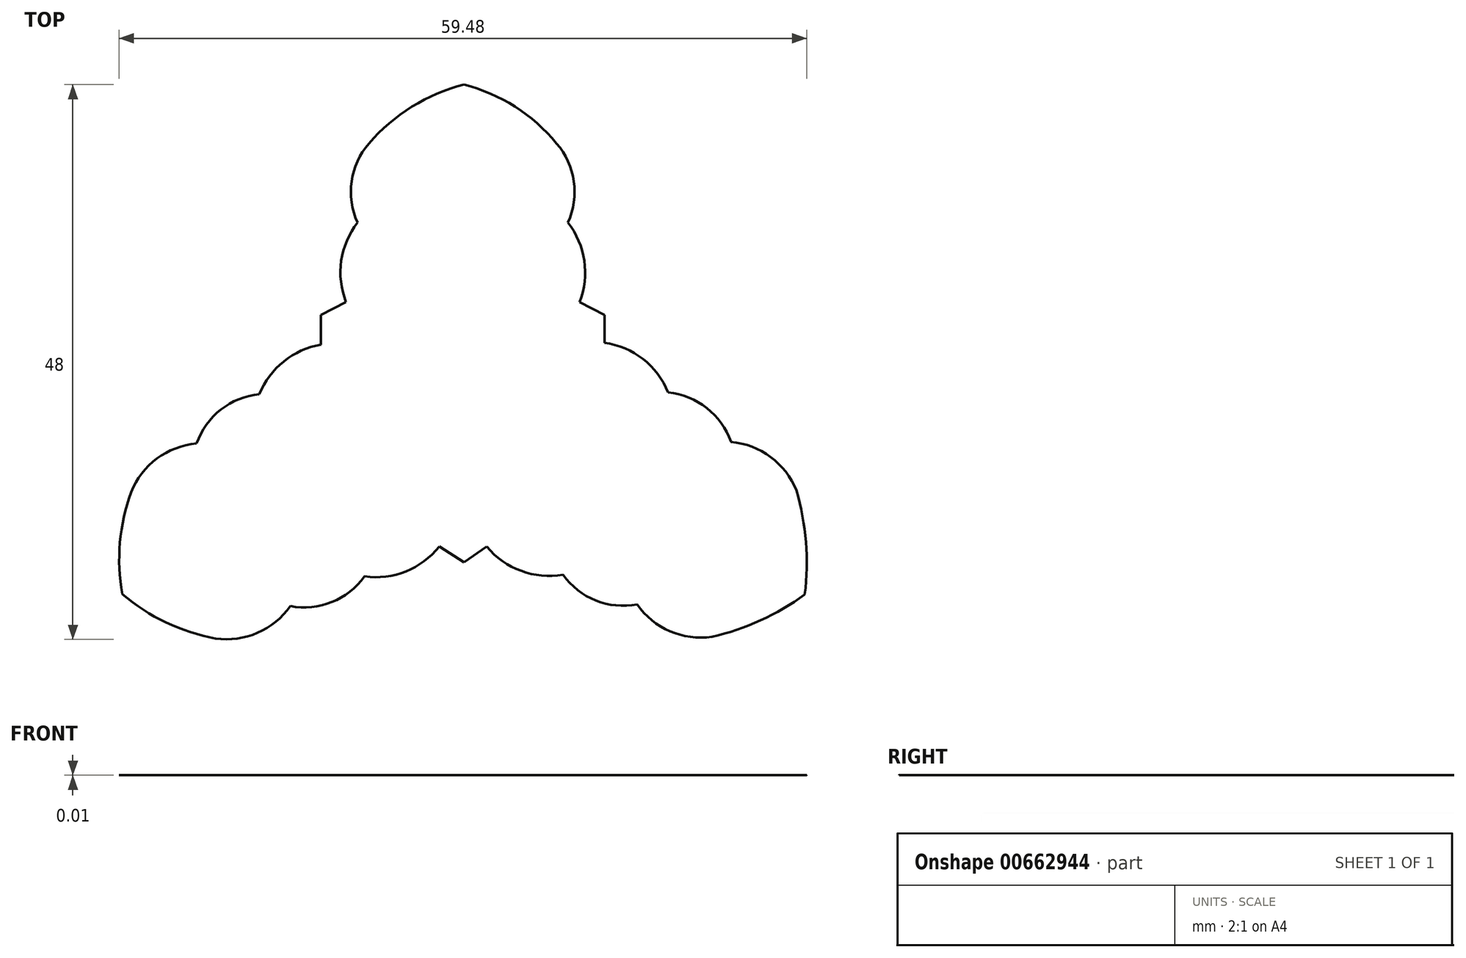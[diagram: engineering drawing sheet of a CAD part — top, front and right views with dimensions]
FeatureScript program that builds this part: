
annotation { "Feature Type Name" : "Feature", "Feature Type Description" : "" }
export const myFeature = defineFeature(function(context is Context, id is Id, definition is map)
    precondition{}
    {
        {
            var Q0;
            Q0=qCreatedBy(makeId("Top.planeOp"),FACE);
            var sketch = newSketch(context, id + "F0", { "sketchPlane" : qUnion([Q0])});
            skPoint(sketch, "E0.center", {"position": v(0, 0) * mm});
            skArc(sketch, "E1", {"start": v(-8.23, 21.98) * mm, "mid": v(-9.72, 18.7) * mm, "end": v(-9.2, 15.13) * mm});
            skArc(sketch, "E2", {"start": v(-9.2, 15.13) * mm, "mid": v(-10.62, 11.82) * mm, "end": v(-10.2, 8.25) * mm});
            skLineSegment(sketch, "E3", {"start": v(-10.2, 8.25) * mm, "end": v(-12.37, 7.15) * mm});
            skLineSegment(sketch, "E4", {"start": v(-12.37, 7.15) * mm, "end": v(-12.37, 4.64) * mm});
            skLineSegment(sketch, "E5.MirrorCS", {"start": v(12.16, 7.15) * mm, "end": v(12.16, 4.64) * mm});
            skLineSegment(sketch, "E6.MirrorCS", {"start": v(10, 8.25) * mm, "end": v(12.16, 7.15) * mm});
            skArc(sketch, "E7.MirrorCS", {"start": v(9, 15.13) * mm, "mid": v(10.4, 11.82) * mm, "end": v(10, 8.25) * mm});
            skArc(sketch, "E8.MirrorCS", {"start": v(8.01, 21.98) * mm, "mid": v(9.5, 18.7) * mm, "end": v(9, 15.13) * mm});
            skArc(sketch, "E9", {"start": v(28.76, -8.05) * mm, "mid": v(26.53, -5.15) * mm, "end": v(23.1, -3.85) * mm});
            skArc(sketch, "E10", {"start": v(23.1, -3.85) * mm, "mid": v(21, -0.92) * mm, "end": v(17.66, 0.43) * mm});
            skArc(sketch, "E11", {"start": v(17.66, 0.43) * mm, "mid": v(15.48, 3.32) * mm, "end": v(12.16, 4.74) * mm});
            skArc(sketch, "E12.MirrorCS", {"start": v(8.56, -15.34) * mm, "mid": v(4.94, -15) * mm, "end": v(1.97, -12.9) * mm});
            skArc(sketch, "E13.MirrorCS", {"start": v(14.98, -17.91) * mm, "mid": v(11.4, -17.56) * mm, "end": v(8.56, -15.34) * mm});
            skArc(sketch, "E14.MirrorCS", {"start": v(21.45, -20.71) * mm, "mid": v(17.82, -20.23) * mm, "end": v(14.98, -17.91) * mm});
            skLineSegment(sketch, "E15", {"start": v(1.97, -12.9) * mm, "end": v(0, -14.26) * mm});
            skLineSegment(sketch, "E16", {"start": v(0, -14.26) * mm, "end": v(-2.14, -12.9) * mm});
            skArc(sketch, "E17", {"start": v(-21.5, -20.86) * mm, "mid": v(-17.86, -20.37) * mm, "end": v(-15.02, -18.05) * mm});
            skArc(sketch, "E18", {"start": v(-15.02, -18.05) * mm, "mid": v(-11.43, -17.7) * mm, "end": v(-8.6, -15.48) * mm});
            skArc(sketch, "E19", {"start": v(-8.6, -15.48) * mm, "mid": v(-5.03, -15.05) * mm, "end": v(-2.14, -12.9) * mm});
            skArc(sketch, "E20.MirrorCS", {"start": v(-17.7, 0.28) * mm, "mid": v(-15.6, 3.12) * mm, "end": v(-12.37, 4.57) * mm});
            skArc(sketch, "E21.MirrorCS", {"start": v(-23.14, -4) * mm, "mid": v(-21.05, -1.06) * mm, "end": v(-17.7, 0.28) * mm});
            skArc(sketch, "E22.MirrorCS", {"start": v(-28.8, -8.2) * mm, "mid": v(-26.56, -5.3) * mm, "end": v(-23.14, -4) * mm});
            skLineSegment(sketch, "E23", {"start": v(-12.37, 4.64) * mm, "end": v(-12.37, 4.57) * mm});
            skArc(sketch, "E24", {"start": v(21.45, -20.71) * mm, "mid": v(25.66, -19.3) * mm, "end": v(29.48, -17.04) * mm});
            skArc(sketch, "E25", {"start": v(29.48, -17.04) * mm, "mid": v(29.58, -12.51) * mm, "end": v(28.76, -8.05) * mm});
            skArc(sketch, "E26", {"start": v(-28.8, -8.2) * mm, "mid": v(-29.77, -12.56) * mm, "end": v(-29.56, -17.02) * mm});
            skArc(sketch, "E27", {"start": v(-29.56, -17.02) * mm, "mid": v(-25.78, -19.47) * mm, "end": v(-21.5, -20.86) * mm});
            skArc(sketch, "E28", {"start": v(0, 27.07) * mm, "mid": v(-4.5, 25.16) * mm, "end": v(-8.23, 21.98) * mm});
            skArc(sketch, "E29", {"start": v(8.01, 21.98) * mm, "mid": v(4.42, 25.17) * mm, "end": v(0, 27.07) * mm});
            skSolve(sketch);
        }
        {
            var Q0;
            Q0=makeQuery(id+"F0.imprint","IMPRINT",FACE,{"disambiguationData":[TD([[makeQuery(id+"F0.imprint","IMPRINT",EDGE,{"derivedFrom":sQuery(id+"F0.wireOp",EDGE,"E1")}),1.0]])]});
            extrude(context, id + "F1", {"entities" : qUnion([Q0]), "depth" : 6 / 406.4 * mm, "offsetDistance" : 25.4 * mm});
        }
    });
